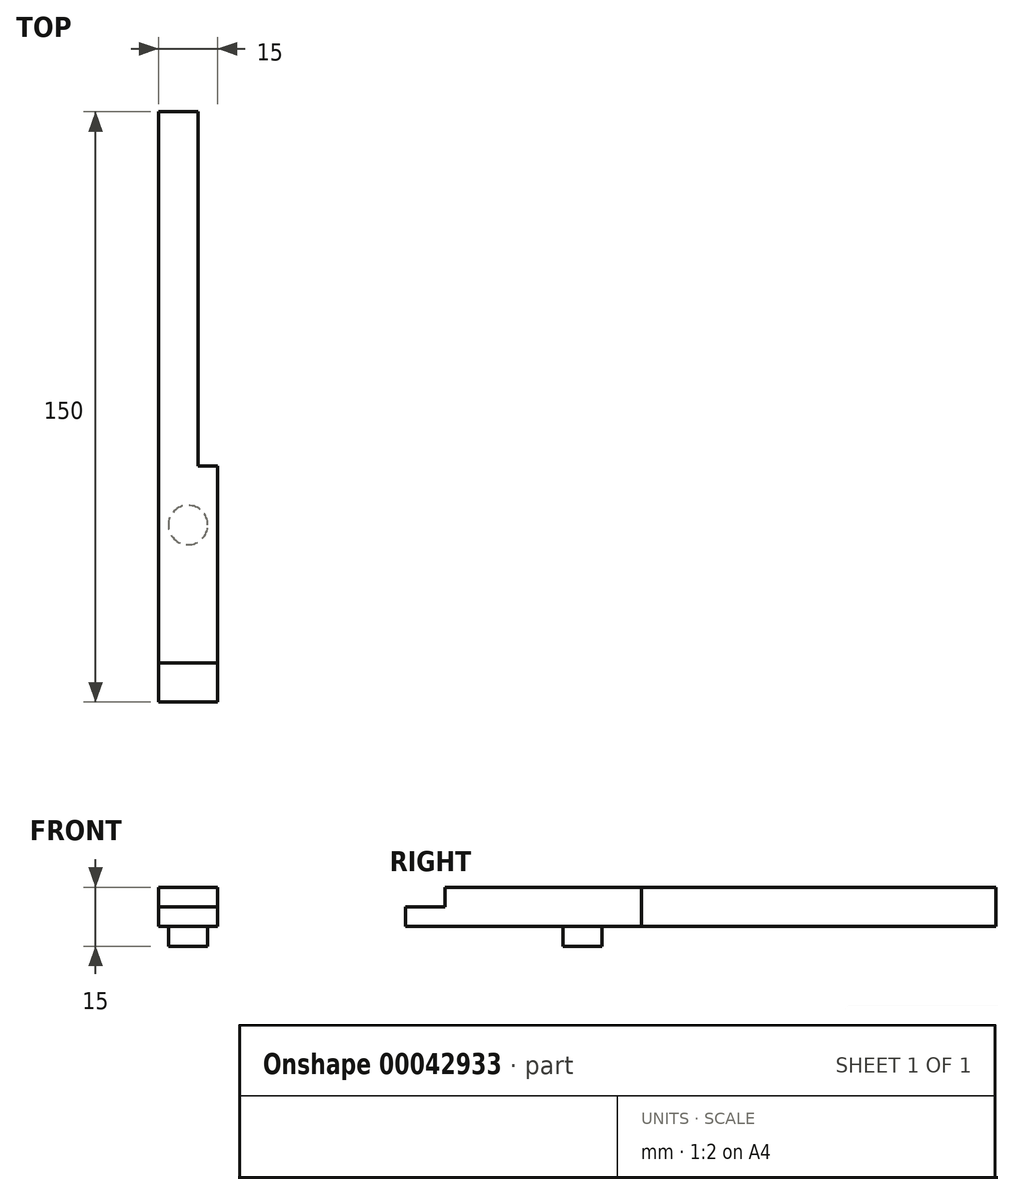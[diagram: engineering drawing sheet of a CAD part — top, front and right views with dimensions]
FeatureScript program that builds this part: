
annotation { "Feature Type Name" : "Feature", "Feature Type Description" : "" }
export const myFeature = defineFeature(function(context is Context, id is Id, definition is map)
    precondition{}
    {
        {
            var Q0;
            Q0=qCreatedBy(makeId("Top.planeOp"),FACE);
            var sketch = newSketch(context, id + "F0", { "sketchPlane" : qUnion([Q0])});
            skLineSegment(sketch, "E0.bottom", {"start": v(0, 0) * mm, "end": v(15, 0) * mm});
            skLineSegment(sketch, "E0.top", {"start": v(0, -150) * mm, "end": v(15, -150) * mm});
            skLineSegment(sketch, "E0.left", {"start": v(0, 0) * mm, "end": v(0, -150) * mm});
            skLineSegment(sketch, "E0.right", {"start": v(15, 0) * mm, "end": v(15, -150) * mm});
            skSolve(sketch);
        }
        {
            var Q0;
            Q0=makeQuery(id+"F0.imprint","IMPRINT",FACE,{"disambiguationData":[TD([[makeQuery(id+"F0.imprint","IMPRINT",EDGE,{"derivedFrom":sQuery(id+"F0.wireOp",EDGE,"E0.bottom")}),-1.0]])]});
            extrude(context, id + "F1", {"entities" : qUnion([Q0]), "oppositeDirection" : true, "depth" : 10 * mm});
        }
        {
            var Q0;
            Q0=makeQuery(id+"F1.opExtrude","SWEPT_FACE",FACE,{"disambiguationData":[OSD([sQuery(id+"F0.wireOp",EDGE,"E0.right")])]});
            var sketch = newSketch(context, id + "F2", { "sketchPlane" : qUnion([Q0])});
            skLineSegment(sketch, "E1.bottom", {"start": v(-150, 0) * mm, "end": v(-140, 0) * mm});
            skLineSegment(sketch, "E1.top", {"start": v(-150, -5) * mm, "end": v(-140, -5) * mm});
            skLineSegment(sketch, "E1.left", {"start": v(-150, 0) * mm, "end": v(-150, -5) * mm});
            skLineSegment(sketch, "E1.right", {"start": v(-140, 0) * mm, "end": v(-140, -5) * mm});
            skSolve(sketch);
        }
        {
            var Q0;
            Q0=makeQuery(id+"F2.imprint","IMPRINT",FACE,{"disambiguationData":[TD([[makeQuery(id+"F2.imprint","IMPRINT",EDGE,{"derivedFrom":sQuery(id+"F2.wireOp",EDGE,"E1.bottom")}),1.0]])]});
            extrude(context, id + "F3", {"entities" : qUnion([Q0]), "operationType" : NewBodyOperationType.REMOVE, "oppositeDirection" : true, "depth" : 15 * mm});
        }
        {
            var Q0;
            Q0=makeQuery(id+"F1.opExtrude","CAP_FACE",FACE,{"disambiguationData":[OSD([sQuery(id+"F0.wireOp",EDGE,"E0.bottom"),sQuery(id+"F0.wireOp",EDGE,"E0.top"),sQuery(id+"F0.wireOp",EDGE,"E0.left"),sQuery(id+"F0.wireOp",EDGE,"E0.right")])],"isStart":false});
            var sketch = newSketch(context, id + "F4", { "sketchPlane" : qUnion([Q0])});
            skLineSegment(sketch, "E2.bottom", {"start": v(15, 0) * mm, "end": v(10, 0) * mm});
            skLineSegment(sketch, "E2.top", {"start": v(15, 90) * mm, "end": v(10, 90) * mm});
            skLineSegment(sketch, "E2.left", {"start": v(15, 0) * mm, "end": v(15, 90) * mm});
            skLineSegment(sketch, "E2.right", {"start": v(10, 0) * mm, "end": v(10, 90) * mm});
            skSolve(sketch);
        }
        {
            var Q0;
            Q0=makeQuery(id+"F4.imprint","IMPRINT",FACE,{"disambiguationData":[TD([[makeQuery(id+"F4.imprint","IMPRINT",EDGE,{"derivedFrom":sQuery(id+"F4.wireOp",EDGE,"E2.bottom")}),1.0]])]});
            extrude(context, id + "F5", {"entities" : qUnion([Q0]), "operationType" : NewBodyOperationType.REMOVE, "oppositeDirection" : true, "depth" : 10 * mm});
        }
        {
            var Q0;
            Q0=makeQuery(id+"F1.opExtrude","CAP_FACE",FACE,{"disambiguationData":[OSD([sQuery(id+"F0.wireOp",EDGE,"E0.bottom"),sQuery(id+"F0.wireOp",EDGE,"E0.top"),sQuery(id+"F0.wireOp",EDGE,"E0.left"),sQuery(id+"F0.wireOp",EDGE,"E0.right")])],"isStart":false});
            var sketch = newSketch(context, id + "F6", { "sketchPlane" : qUnion([Q0])});
            skLineSegment(sketch, "E3.bottom", {"start": v(15, 90) * mm, "end": v(0, 90) * mm});
            skLineSegment(sketch, "E3.top", {"start": v(15, 150) * mm, "end": v(0, 150) * mm});
            skLineSegment(sketch, "E3.left", {"start": v(15, 90) * mm, "end": v(15, 150) * mm});
            skLineSegment(sketch, "E3.right", {"start": v(0, 90) * mm, "end": v(0, 150) * mm});
            skLineSegment(sketch, "E4.left", {"start": v(15, 120) * mm, "end": v(15, 90) * mm});
            skLineSegment(sketch, "E4.right", {"start": v(0, 120) * mm, "end": v(0, 90) * mm});
            skPoint(sketch, "E5", {"position": v(7.5, 105) * mm});
            skCircle(sketch, "E6", {"center": v(7.5, 105) * mm, "radius": 5 * mm});
            skSolve(sketch);
        }
        {
            var Q0;
            Q0=makeQuery(id+"F6.imprint","IMPRINT",FACE,{"disambiguationData":[TD([[makeQuery(id+"F6.imprint","IMPRINT",EDGE,{"derivedFrom":sQuery(id+"F6.wireOp",EDGE,"E6")}),1.0]])]});
            extrude(context, id + "F7", {"entities" : qUnion([Q0]), "operationType" : NewBodyOperationType.ADD, "depth" : 5 * mm});
        }
    });
